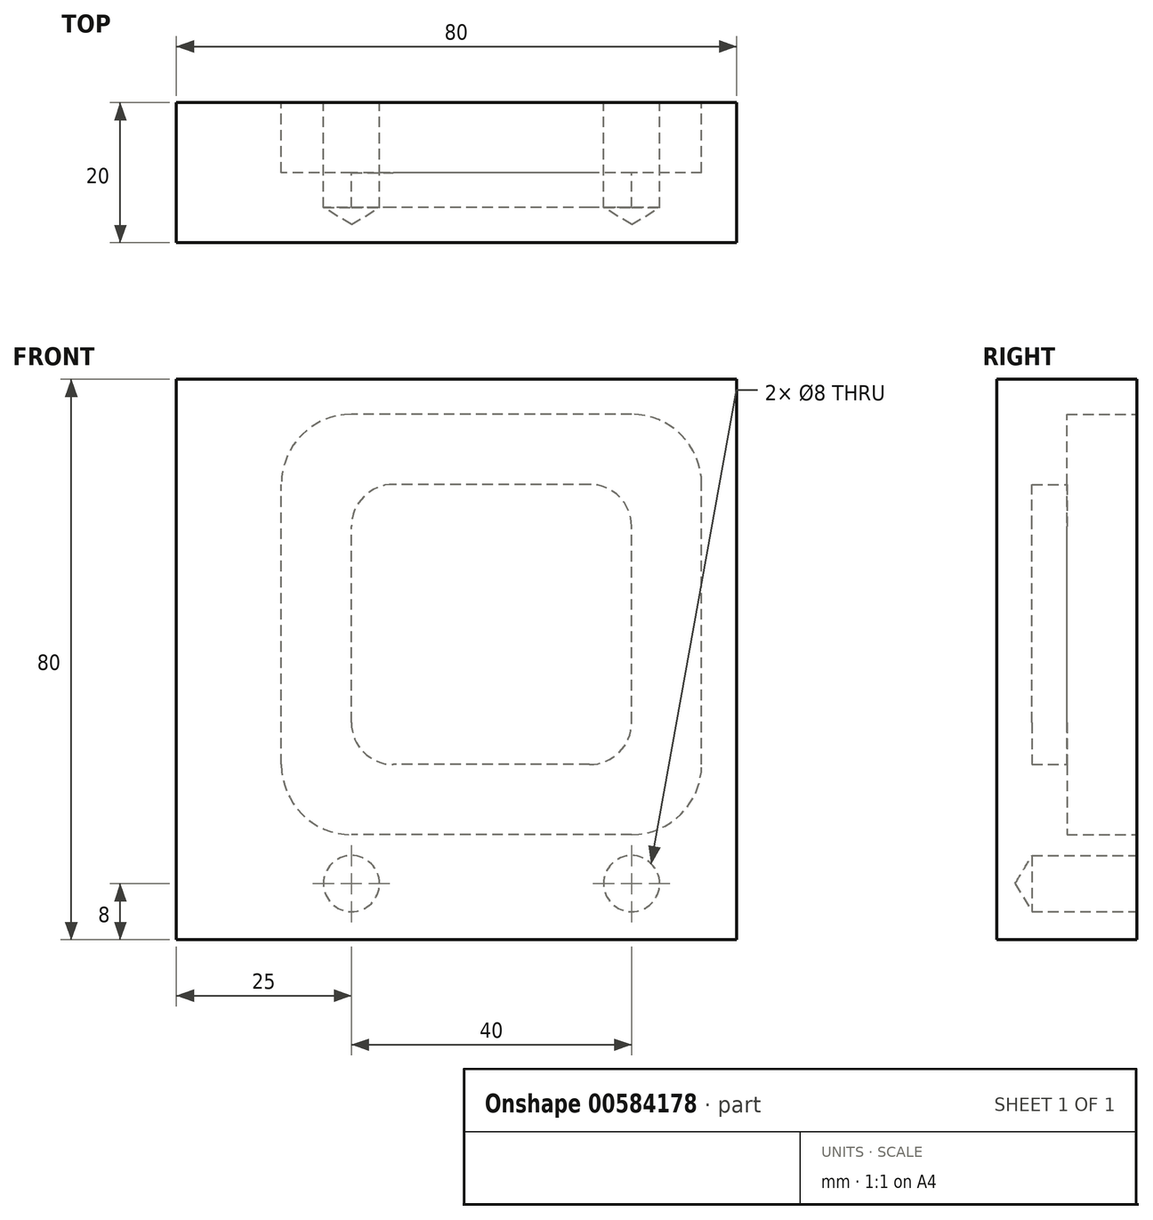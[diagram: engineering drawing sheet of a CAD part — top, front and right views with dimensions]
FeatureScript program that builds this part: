
annotation { "Feature Type Name" : "Feature", "Feature Type Description" : "" }
export const myFeature = defineFeature(function(context is Context, id is Id, definition is map)
    precondition{}
    {
        {
            var Q0;
            Q0=qCreatedBy(makeId("Front.planeOp"),FACE);
            var sketch = newSketch(context, id + "F0", { "sketchPlane" : qUnion([Q0])});
            skLineSegment(sketch, "E0.bottom", {"start": v(1010.53, -1114.78) * mm, "end": v(-1021.47, -1114.78) * mm});
            skLineSegment(sketch, "E0.top", {"start": v(1010.53, 1125.14) * mm, "end": v(-1021.47, 1125.14) * mm});
            skLineSegment(sketch, "E0.left", {"start": v(1010.53, -1114.78) * mm, "end": v(1010.53, 1125.14) * mm});
            skLineSegment(sketch, "E0.right", {"start": v(-1021.47, -1114.78) * mm, "end": v(-1021.47, 1125.14) * mm});
            skLineSegment(sketch, "E1.bottom", {"start": v(40, -40) * mm, "end": v(-40, -40) * mm});
            skLineSegment(sketch, "E1.top", {"start": v(40, 40) * mm, "end": v(-40, 40) * mm});
            skLineSegment(sketch, "E1.left", {"start": v(40, -40) * mm, "end": v(40, 40) * mm});
            skLineSegment(sketch, "E1.right", {"start": v(-40, -40) * mm, "end": v(-40, 40) * mm});
            skSolve(sketch);
        }
        {
            var Q0;
            Q0=makeQuery(id+"F0.imprint","IMPRINT",FACE,{"disambiguationData":[TD([[makeQuery(id+"F0.imprint","IMPRINT",EDGE,{"derivedFrom":sQuery(id+"F0.wireOp",EDGE,"E1.bottom")}),-1.0]])]});
            extrude(context, id + "F1", {"entities" : qUnion([Q0]), "depth" : 20 * mm, "offsetDistance" : 25 * mm});
        }
        {
            var Q0;
            Q0=makeQuery(id+"F1.opExtrude","CAP_FACE",FACE,{"disambiguationData":[OSD([sQuery(id+"F0.wireOp",EDGE,"E1.bottom"),sQuery(id+"F0.wireOp",EDGE,"E1.top"),sQuery(id+"F0.wireOp",EDGE,"E1.left"),sQuery(id+"F0.wireOp",EDGE,"E1.right")])],"isStart":true});
            var sketch = newSketch(context, id + "F2", { "sketchPlane" : qUnion([Q0])});
            skLineSegment(sketch, "E2.bottom", {"start": v(-25, -25) * mm, "end": v(15, -25) * mm});
            skLineSegment(sketch, "E2.top", {"start": v(-25, 35) * mm, "end": v(15, 35) * mm});
            skLineSegment(sketch, "E2.left", {"start": v(-35, -15) * mm, "end": v(-35, 25) * mm});
            skLineSegment(sketch, "E2.right", {"start": v(25, -15) * mm, "end": v(25, 25) * mm});
            skPoint(sketch, "E3.visualSharp", {"position": v(-35, 35) * mm});
            skArc(sketch, "E3.filletArc", {"start": v(-25, 35) * mm, "mid": v(-32.07, 32.07) * mm, "end": v(-35, 25) * mm});
            skPoint(sketch, "E4.visualSharp", {"position": v(-35, -25) * mm});
            skArc(sketch, "E4.filletArc", {"start": v(-35, -15) * mm, "mid": v(-32.07, -22.07) * mm, "end": v(-25, -25) * mm});
            skPoint(sketch, "E5.visualSharp", {"position": v(25, -25) * mm});
            skArc(sketch, "E5.filletArc", {"start": v(15, -25) * mm, "mid": v(22.07, -22.07) * mm, "end": v(25, -15) * mm});
            skPoint(sketch, "E6.visualSharp", {"position": v(25, 35) * mm});
            skArc(sketch, "E6.filletArc", {"start": v(25, 25) * mm, "mid": v(22.07, 32.07) * mm, "end": v(15, 35) * mm});
            skSolve(sketch);
        }
        {
            var Q0;
            Q0=makeQuery(id+"F2.imprint","IMPRINT",FACE,{"disambiguationData":[TD([[makeQuery(id+"F2.imprint","IMPRINT",EDGE,{"derivedFrom":sQuery(id+"F2.wireOp",EDGE,"E2.bottom")}),1.0]])]});
            extrude(context, id + "F3", {"entities" : qUnion([Q0]), "operationType" : NewBodyOperationType.REMOVE, "oppositeDirection" : true, "depth" : 10 * mm, "offsetDistance" : 25 * mm});
        }
        {
            var Q0;
            Q0=makeQuery(id+"F3.boolean.opBoolean","COPY",FACE,{"derivedFrom":makeQuery(id+"F3.opExtrude","CAP_FACE",FACE,{"disambiguationData":[OSD([sQuery(id+"F2.wireOp",EDGE,"E2.bottom"),sQuery(id+"F2.wireOp",EDGE,"E2.top"),sQuery(id+"F2.wireOp",EDGE,"E2.left"),sQuery(id+"F2.wireOp",EDGE,"E2.right"),sQuery(id+"F2.wireOp",EDGE,"E3.filletArc"),sQuery(id+"F2.wireOp",EDGE,"E4.filletArc"),sQuery(id+"F2.wireOp",EDGE,"E5.filletArc"),sQuery(id+"F2.wireOp",EDGE,"E6.filletArc")])],"isStart":false})});
            var sketch = newSketch(context, id + "F4", { "sketchPlane" : qUnion([Q0])});
            skLineSegment(sketch, "E7.bottom", {"start": v(-19, -15) * mm, "end": v(9, -15) * mm});
            skLineSegment(sketch, "E7.top", {"start": v(-19, 25) * mm, "end": v(9, 25) * mm});
            skLineSegment(sketch, "E7.left", {"start": v(-25, -9) * mm, "end": v(-25, 19) * mm});
            skLineSegment(sketch, "E7.right", {"start": v(15, -9) * mm, "end": v(15, 19) * mm});
            skPoint(sketch, "E8.visualSharp", {"position": v(-25, 25) * mm});
            skArc(sketch, "E8.filletArc", {"start": v(-19, 25) * mm, "mid": v(-23.24, 23.24) * mm, "end": v(-25, 19) * mm});
            skPoint(sketch, "E9.visualSharp", {"position": v(-25, -15) * mm});
            skArc(sketch, "E9.filletArc", {"start": v(-25, -9) * mm, "mid": v(-23.24, -13.24) * mm, "end": v(-19, -15) * mm});
            skPoint(sketch, "E10.visualSharp", {"position": v(15, -15) * mm});
            skArc(sketch, "E10.filletArc", {"start": v(9, -15) * mm, "mid": v(13.24, -13.24) * mm, "end": v(15, -9) * mm});
            skPoint(sketch, "E11.visualSharp", {"position": v(15, 25) * mm});
            skArc(sketch, "E11.filletArc", {"start": v(15, 19) * mm, "mid": v(13.24, 23.24) * mm, "end": v(9, 25) * mm});
            skSolve(sketch);
        }
        {
            var Q0;
            Q0=makeQuery(id+"F4.imprint","IMPRINT",FACE,{"disambiguationData":[TD([[makeQuery(id+"F4.imprint","IMPRINT",EDGE,{"derivedFrom":sQuery(id+"F4.wireOp",EDGE,"E7.bottom")}),1.0]])]});
            extrude(context, id + "F5", {"entities" : qUnion([Q0]), "operationType" : NewBodyOperationType.REMOVE, "oppositeDirection" : true, "depth" : 5 * mm, "offsetDistance" : 25 * mm});
        }
        {
            var Q0;
            Q0=makeQuery(id+"F1.opExtrude","CAP_FACE",FACE,{"disambiguationData":[OSD([sQuery(id+"F0.wireOp",EDGE,"E1.bottom"),sQuery(id+"F0.wireOp",EDGE,"E1.top"),sQuery(id+"F0.wireOp",EDGE,"E1.left"),sQuery(id+"F0.wireOp",EDGE,"E1.right")])],"isStart":true});
            var sketch = newSketch(context, id + "F6", { "sketchPlane" : qUnion([Q0])});
            skCircle(sketch, "E12", {"center": v(-25, -32) * mm, "radius": 4 * mm});
            skCircle(sketch, "E13", {"center": v(15, -32) * mm, "radius": 4 * mm});
            skSolve(sketch);
        }
        {
            var Q0;
            Q0=sQuery(id+"F6.wireOp",VERTEX,"E12.center");
            var Q1;
            Q1=sQuery(id+"F6.wireOp",VERTEX,"E13.center");
            var Q2;
            Q2=makeQuery(id+"F1.opExtrude","SWEPT_BODY",BODY,{"disambiguationData":[OSD([sQuery(id+"F0.wireOp",EDGE,"E1.bottom"),sQuery(id+"F0.wireOp",EDGE,"E1.top"),sQuery(id+"F0.wireOp",EDGE,"E1.left"),sQuery(id+"F0.wireOp",EDGE,"E1.right")])]});
            hole(context, id + "F7", {"style" : HoleStyle.SIMPLE, "endStyle" : HoleEndStyle.BLIND, "holeDiameter" : 8 * mm, "majorDiameter" : 5 * mm, "holeDepth" : 15 * mm, "isTappedThrough" : true, "tappedDepth" : 12 * mm, "tapClearance" : 3, "locations" : qUnion([Q0, Q1]), "scope" : qUnion([Q2])});
        }
    });
